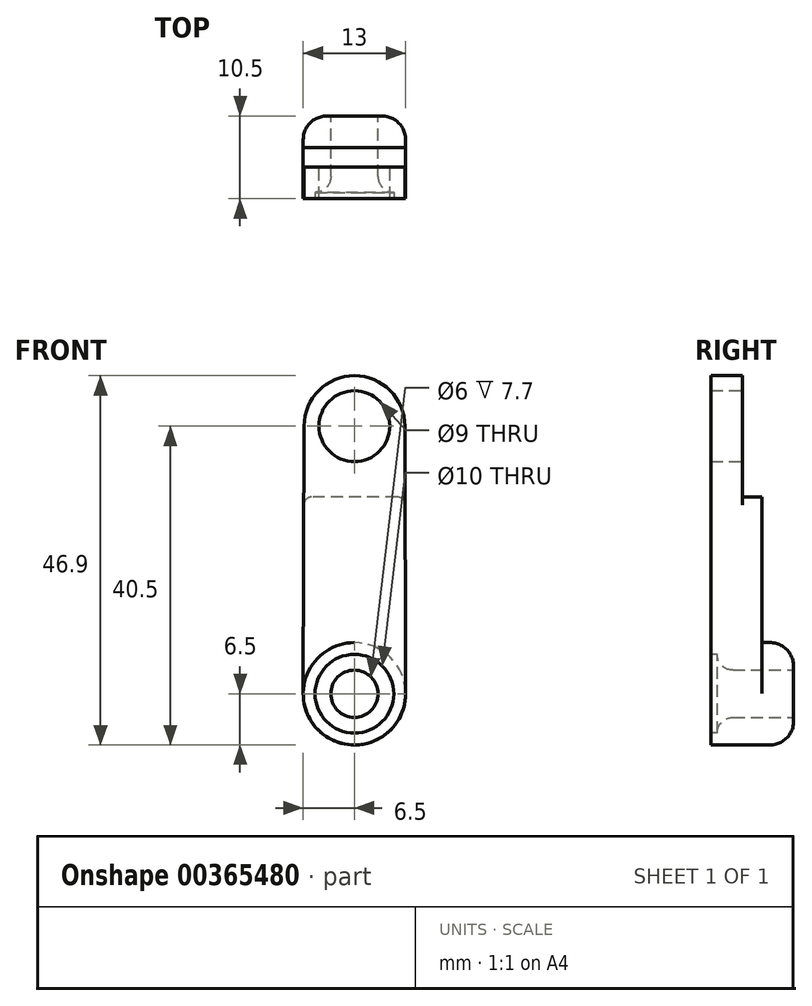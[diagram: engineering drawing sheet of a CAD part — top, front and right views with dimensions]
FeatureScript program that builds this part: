
annotation { "Feature Type Name" : "Feature", "Feature Type Description" : "" }
export const myFeature = defineFeature(function(context is Context, id is Id, definition is map)
    precondition{}
    {
        {
            var Q0;
            Q0=qCreatedBy(makeId("Front.planeOp"),FACE);
            var sketch = newSketch(context, id + "F0", { "sketchPlane" : qUnion([Q0])});
            skCircle(sketch, "E0", {"center": v(0, 0) * mm, "radius": 4.5 * mm});
            skArc(sketch, "E1", {"start": v(6.4, 0) * mm, "mid": v(0, 6.4) * mm, "end": v(-6.4, 0) * mm});
            skCircle(sketch, "E2", {"center": v(0, -34) * mm, "radius": 3 * mm});
            skArc(sketch, "E3", {"start": v(-6.5, -33.96) * mm, "mid": v(0, -40.5) * mm, "end": v(6.5, -33.96) * mm});
            skLineSegment(sketch, "E4", {"start": v(-6.4, 0) * mm, "end": v(-6.5, -34) * mm});
            skLineSegment(sketch, "E5.MirrorCS", {"start": v(6.4, 0) * mm, "end": v(6.5, -34) * mm});
            skSolve(sketch);
        }
        {
            var Q0;
            Q0 = qSketchRegion(id + "F0", true);
            extrude(context, id + "F1", {"entities" : qUnion([Q0]), "depth" : 4 * mm});
        }
        {
            var Q0;
            Q0=makeQuery(id+"F1.opExtrude","CAP_FACE",FACE,{"disambiguationData":[OSD([sQuery(id+"F0.wireOp",EDGE,"E0"),sQuery(id+"F0.wireOp",EDGE,"E1"),sQuery(id+"F0.wireOp",EDGE,"E2"),sQuery(id+"F0.wireOp",EDGE,"E3"),sQuery(id+"F0.wireOp",EDGE,"E4"),sQuery(id+"F0.wireOp",EDGE,"E5.MirrorCS")])],"isStart":false});
            var sketch = newSketch(context, id + "F2", { "sketchPlane" : qUnion([Q0])});
            skSolve(sketch);
        }
        {
            var Q0;
            Q0=makeQuery(id+"F1.opExtrude","CAP_FACE",FACE,{"disambiguationData":[OSD([sQuery(id+"F0.wireOp",EDGE,"E0"),sQuery(id+"F0.wireOp",EDGE,"E1"),sQuery(id+"F0.wireOp",EDGE,"E2"),sQuery(id+"F0.wireOp",EDGE,"E3"),sQuery(id+"F0.wireOp",EDGE,"E4"),sQuery(id+"F0.wireOp",EDGE,"E5.MirrorCS")])],"isStart":true});
            var sketch = newSketch(context, id + "F3", { "sketchPlane" : qUnion([Q0])});
            skCircle(sketch, "E6", {"center": v(0, -34) * mm, "radius": 6.5 * mm});
            skCircle(sketch, "E7", {"center": v(0, -34) * mm, "radius": 3 * mm});
            skSolve(sketch);
        }
        {
            var Q0;
            Q0 = qSketchRegion(id + "F3", true);
            extrude(context, id + "F4", {"entities" : qUnion([Q0]), "operationType" : NewBodyOperationType.ADD, "depth" : 6.5 * mm});
        }
        {
            var Q0;
            Q0=makeQuery(id+"F2.imprint","IMPRINT",FACE,{"disambiguationData":[TD([[makeQuery(id+"F2.imprint","IMPRINT",EDGE,{"derivedFrom":makeQuery(id+"F1.opExtrude","CAP_EDGE",EDGE,{"disambiguationData":[OSD([sQuery(id+"F0.wireOp",EDGE,"E0")])],"isStart":false})}),-1.0]])]});
            var sketch = newSketch(context, id + "F5", { "sketchPlane" : qUnion([Q0])});
            skLineSegment(sketch, "E8", {"start": v(0, 0) * mm, "end": v(0, -34) * mm});
            skCircle(sketch, "E9", {"center": v(0, -34) * mm, "radius": 5 * mm});
            skSolve(sketch);
        }
        {
            var Q0;
            Q0 = qSketchRegion(id + "F5", true);
            extrude(context, id + "F6", {"entities" : qUnion([Q0]), "operationType" : NewBodyOperationType.REMOVE, "oppositeDirection" : true, "depth" : 0.8 * mm});
        }
        {
            var Q0;
            Q0=makeQuery(id+"F6.boolean.opBoolean","INTERSECT",EDGE,{"derivedFrom":[makeQuery(id+"F4.boolean.opBoolean","MERGE",FACE,{"derivedFrom":[makeQuery(id+"F1.opExtrude","SWEPT_FACE",FACE,{"disambiguationData":[OSD([sQuery(id+"F0.wireOp",EDGE,"E2")])]}),makeQuery(id+"F4.opExtrude","SWEPT_FACE",FACE,{"disambiguationData":[OSD([sQuery(id+"F3.wireOp",EDGE,"E7")])]})]}),makeQuery(id+"F6.opExtrude","CAP_FACE",FACE,{"disambiguationData":[OSD([sQuery(id+"F5.wireOp",EDGE,"E9")])],"isStart":false})]});
            fillet(context, id + "F7", {"entities" : qUnion([Q0]), "radius" : 2 * mm, "tangentPropagation" : true, "allowEdgeOverflow" : false});
        }
        {
            var Q0;
            Q0=makeQuery(id+"F1.opExtrude","CAP_FACE",FACE,{"disambiguationData":[OSD([sQuery(id+"F0.wireOp",EDGE,"E0"),sQuery(id+"F0.wireOp",EDGE,"E1"),sQuery(id+"F0.wireOp",EDGE,"E2"),sQuery(id+"F0.wireOp",EDGE,"E3"),sQuery(id+"F0.wireOp",EDGE,"E4"),sQuery(id+"F0.wireOp",EDGE,"E5.MirrorCS")])],"isStart":true});
            var sketch = newSketch(context, id + "F8", { "sketchPlane" : qUnion([Q0])});
            skLineSegment(sketch, "E10", {"start": v(-5.07, -30.47) * mm, "end": v(4.99, -30.47) * mm});
            skPoint(sketch, "E11.start.orphan", {"position": v(0, -34) * mm});
            skCircle(sketch, "E12", {"center": v(0, -34) * mm, "radius": 6.5 * mm});
            skLineSegment(sketch, "E13", {"start": v(-6.43, -9) * mm, "end": v(-6.5, -33.96) * mm});
            skLineSegment(sketch, "E14", {"start": v(6.43, -9) * mm, "end": v(6.5, -33.96) * mm});
            skLineSegment(sketch, "E15", {"start": v(-6.5, -33.96) * mm, "end": v(-5.07, -30.47) * mm});
            skLineSegment(sketch, "E16", {"start": v(4.99, -30.47) * mm, "end": v(6.5, -33.96) * mm});
            skLineSegment(sketch, "E17", {"start": v(0, -9) * mm, "end": v(6.43, -9) * mm});
            skLineSegment(sketch, "E18", {"start": v(0, -9) * mm, "end": v(-6.43, -9) * mm});
            skSolve(sketch);
        }
        {
            var Q0;
            Q0 = qSketchRegion(id + "F8", true);
            extrude(context, id + "F9", {"entities" : qUnion([Q0]), "operationType" : NewBodyOperationType.ADD, "depth" : 2.5 * mm});
        }
        {
            var Q0;
            {var subQ0=sQuery(id+"F3.wireOp",EDGE,"E6");Q0=makeQuery(id+"F4.opExtrude","CAP_EDGE",EDGE,{"disambiguationData":[OSD([subQ0]),TDD([makeQuery(id+"F3.imprint","IMPRINT",EDGE,{"disambiguationData":[TD([[makeQuery(id+"F3.imprint","INTERSECT",VERTEX,{"derivedFrom":[makeQuery(id+"F1.opExtrude","CAP_EDGE",EDGE,{"disambiguationData":[OSD([sQuery(id+"F0.wireOp",EDGE,"E5.MirrorCS")])],"isStart":true}),subQ0]}),1.0]])],"derivedFrom":subQ0})])],"isStart":false});}
            fillet(context, id + "F10", {"entities" : qUnion([Q0]), "radius" : 3 * mm, "tangentPropagation" : true, "allowEdgeOverflow" : false});
        }
        {
            var Q0;
            Q0=makeQuery(id+"F9.boolean.opBoolean","SPLIT",FACE,{"disambiguationData":[TD([makeQuery(id+"F1.opExtrude","SWEPT_FACE",FACE,{"disambiguationData":[OSD([sQuery(id+"F0.wireOp",EDGE,"E2")])]})])],"derivedFrom":makeQuery(id+"F9.opExtrude","CAP_FACE",FACE,{"disambiguationData":[OSD([sQuery(id+"F8.wireOp",EDGE,"xkU1GKof-sexN-1Fb5-6Ltp-fYOl9kyFpAs3"),sQuery(id+"F8.wireOp",EDGE,"E12"),sQuery(id+"F8.wireOp",EDGE,"E13"),sQuery(id+"F8.wireOp",EDGE,"E14"),sQuery(id+"F8.wireOp",EDGE,"eeb54527-1bce-47dd-ba79-f9cbb083f104.filletArc"),sQuery(id+"F8.wireOp",EDGE,"0639db36-7a94-4d4c-b69d-a09ca8241c44.filletArc")])],"isStart":false})});
            extrude(context, id + "F11", {"entities" : qUnion([Q0]), "operationType" : NewBodyOperationType.REMOVE, "oppositeDirection" : true, "depth" : 25 * mm});
        }
        {
            var Q0;
            Q0=makeQuery(id+"F9.opExtrude","SWEPT_EDGE",EDGE,{"disambiguationData":[OSD([sQuery(id+"F0.wireOp",EDGE,"E5.MirrorCS"),sQuery(id+"F8.wireOp",EDGE,"E13"),sQuery(id+"F8.wireOp",EDGE,"E18")])]});
            var Q1;
            Q1=makeQuery(id+"F9.opExtrude","SWEPT_EDGE",EDGE,{"disambiguationData":[OSD([sQuery(id+"F0.wireOp",EDGE,"E4"),sQuery(id+"F8.wireOp",EDGE,"E14"),sQuery(id+"F8.wireOp",EDGE,"E17")])]});
            fillet(context, id + "F12", {"entities" : qUnion([Q0, Q1]), "radius" : 1 * mm, "tangentPropagation" : true, "allowEdgeOverflow" : false});
        }
    });
